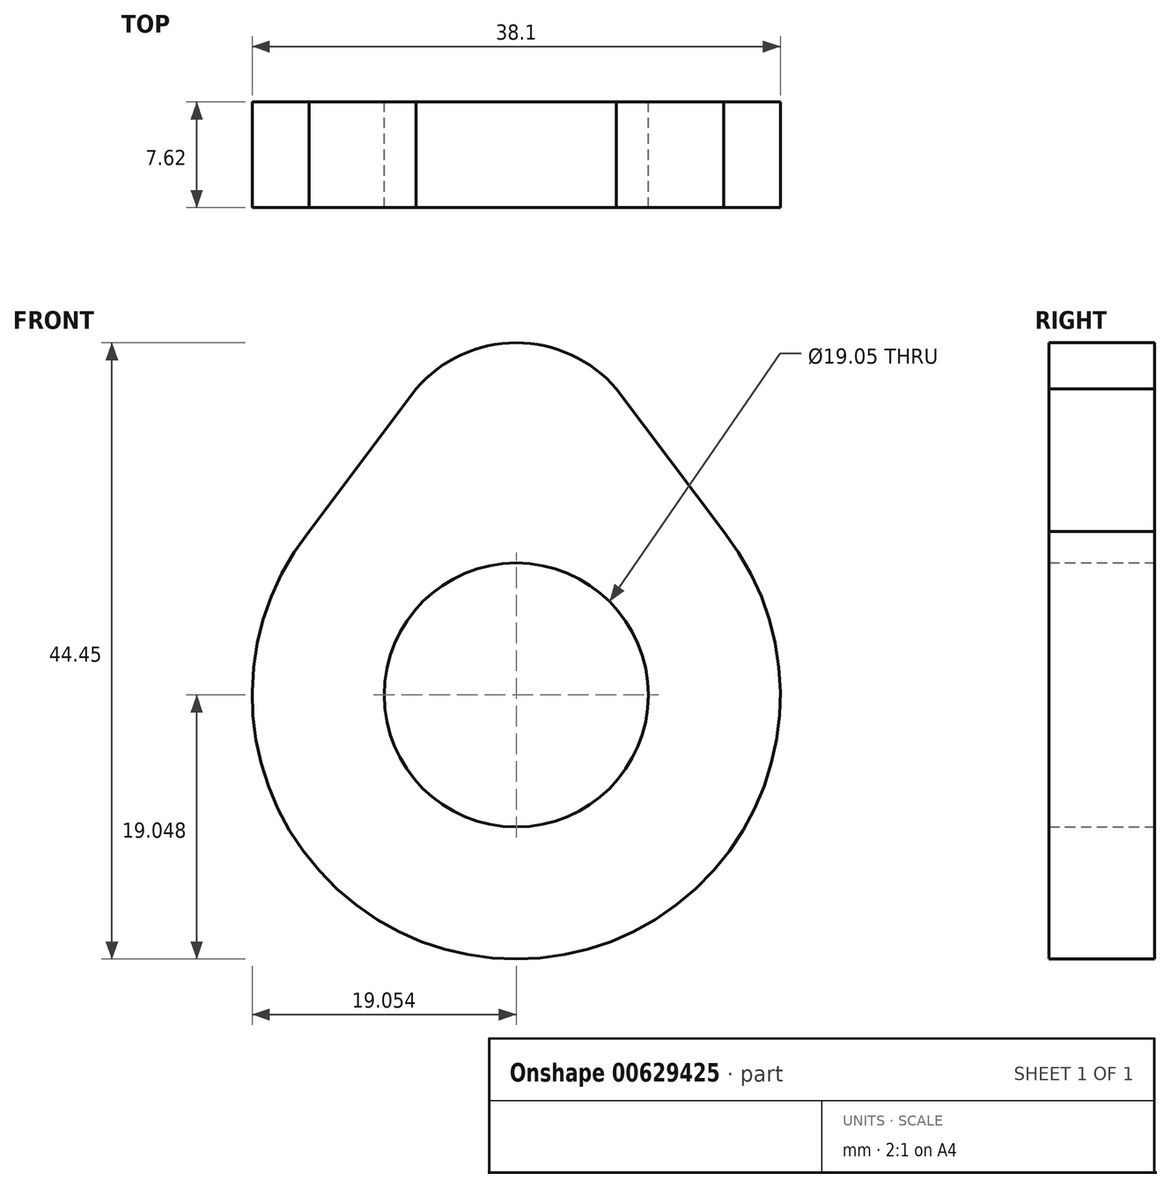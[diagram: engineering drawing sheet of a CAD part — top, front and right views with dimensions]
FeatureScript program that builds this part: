
annotation { "Feature Type Name" : "Feature", "Feature Type Description" : "" }
export const myFeature = defineFeature(function(context is Context, id is Id, definition is map)
    precondition{}
    {
        {
            var Q0;
            Q0=qCreatedBy(makeId("Front.planeOp"),FACE);
            var sketch = newSketch(context, id + "F0", { "sketchPlane" : qUnion([Q0])});
            skArc(sketch, "E0", {"start": v(-47.52, 67.69) * mm, "mid": v(-54.75, 71) * mm, "end": v(-61.97, 67.69) * mm});
            skArc(sketch, "E1", {"start": v(-69.7, 57.4) * mm, "mid": v(-54.75, 26.56) * mm, "end": v(-39.8, 57.4) * mm});
            skLineSegment(sketch, "E2", {"start": v(-69.7, 57.4) * mm, "end": v(-61.97, 67.69) * mm});
            skLineSegment(sketch, "E3", {"start": v(-39.8, 57.4) * mm, "end": v(-47.52, 67.69) * mm});
            skCircle(sketch, "E4", {"center": v(-54.75, 45.6) * mm, "radius": 9.53 * mm});
            skSolve(sketch);
        }
        {
            var Q0;
            Q0=makeQuery(id+"F0.imprint","IMPRINT",FACE,{"disambiguationData":[TD([[makeQuery(id+"F0.imprint","IMPRINT",EDGE,{"derivedFrom":sQuery(id+"F0.wireOp",EDGE,"E0")}),1.0]])]});
            extrude(context, id + "F1", {"entities" : qUnion([Q0]), "depth" : 7.62 * mm, "offsetDistance" : 25.4 * mm});
        }
    });
